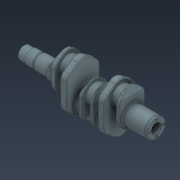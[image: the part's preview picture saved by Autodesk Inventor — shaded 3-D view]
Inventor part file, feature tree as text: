
AUTODESK INVENTOR PART (.ipt)
format: ipt  version: 2022 (Build 260153000, 153)  size: 985,088 bytes
history: native  units: mm
features: sketch x21, extrude x17, plane x4, hole x3, chamfer x3, projected_geometry x3, revolve x2, fillet x2, mirror x2
ambient origin geometry x8: Origin, YZ Plane, XZ Plane, XY Plane, X Axis, Y Axis, Z Axis, Center Point
bodies: Solid1 (feature_tree)
feature tree (57):
  revolve  "Revolution1"  [1 undecoded]
  plane  "Work Plane7"
  sketch  "Sketch22"  dims[d3=44.0mm d4=36.0mm]
  extrude  "Extrusion18"  Depth=36.0mm
  extrude  "Extrusion19"  Depth=42.0mm
  extrude  "Extrusion20"  Depth=2.0mm
  extrude  "Extrusion21"  TaperAngle=90.0deg  [1 undecoded]
  plane  "Work Plane8"
  extrude  "Extrusion22"  Depth=1.0mm
  extrude  "Extrusion23"  Depth=65.0mm
  extrude  "Extrusion24"  Depth=34.5mm
  extrude  "Extrusion25"  Depth=1.0mm TaperAngle=0.0deg
  extrude  "Extrusion26"  Depth=74.0mm
  extrude  "Extrusion27"  Depth=51.2mm
  extrude  "Extrusion28"  Depth=10.0mm TaperAngle=0.0deg
  plane  "Work Plane9"
  extrude  "Extrusion29"  Depth=1.0mm
  extrude  "Extrusion30"  Depth=1.0mm
  fillet  "Fillet1"  Radius=1.0mm
  mirror  "Mirror1"
  mirror  "Mirror2"
  plane  "Work Plane10"
  extrude  "Extrusion32"  Depth=29.9mm
  extrude  "Extrusion33"  Depth=1.0mm TaperAngle=0.0deg
  extrude  "Extrusion34"  Depth=2.0mm
  extrude  "Extrusion35"  Depth=21.0mm TaperAngle=0.0deg
  fillet  "Fillet2"  Radius=1.0mm
  revolve  "Revolution2"  [1 undecoded]
  hole  "Hole1"  [1 undecoded]
  hole  "Hole2"  [1 undecoded]
  hole  "Hole3"  [1 undecoded]
  chamfer  "Chamfer1"  Distance=55.0mm
  chamfer  "Chamfer2"  Distance=21.0mm
  chamfer  "Chamfer3"  Distance=28.965484mm
  sketch  "Sketch1"  dims[d1=23.0mm d2=23.0mm]
  sketch  "Sketch23"  dims[d6=40.0mm d7=42.0mm]
  sketch  "Sketch24"  dims[d9=25.5mm d10=2.0mm]
  sketch  "Sketch25"  dims[d11=1.5mm d12=90.0deg]
  sketch  "Sketch26"  dims[d13=65.0mm d15=1.0mm]
  sketch  "Sketch27"  dims[d96=14.76mm d97=65.0mm]
  sketch  "Sketch28"  dims[d98=55.0mm d99=34.5mm]
  sketch  "Sketch29"  dims[d100=22.0mm d101=0.0mm d102=1.0mm d103=0.0mm]
  sketch  "Sketch30"  dims[d105=15.0mm d106=74.0mm]
  projected_geometry  "Projected Loop9"
  sketch  "Sketch31"  dims[d107=27.2mm d108=51.2mm]
  sketch  "Sketch32"  dims[d109=2.0mm d110=10.0mm d111=0.0mm]
  sketch  "Sketch33"  dims[d112=1.0mm d113=0.0mm d114=18.91mm]
  sketch  "Sketch35"  dims[d115=65.0mm d116=69.0mm d117=1.0mm d118=0.0mm]
  sketch  "Sketch36"  dims[d119=25.0mm d120=29.9mm]
  sketch  "Sketch37"  dims[d122=95.0mm d124=1.0mm d125=0.0mm]
  sketch  "Sketch39"  dims[d126=2.0mm d127=2.0mm]
  projected_geometry  "Projected Loop12"
  projected_geometry  "Projected Loop13"
  sketch  "Sketch40"  dims[d128=55.0mm d129=21.0mm d130=0.0mm d131=1.0mm d132=0.0mm]
  sketch  "Sketch41"  dims[d133=15.0mm d134=25.0mm]
  sketch  "Sketch42"  dims[d135=40.4mm d136=25.0mm]
  sketch  "Sketch43"  dims[d137=10.43mm d138=0.0mm d139=65.0mm d140=1.0mm d141=0.0mm d142=55.0mm d143=21.0mm d144=0.0mm d145=28.965484mm d146=23.0mm d147=0.0mm d148=0.0mm d149=28.965484mm d150=8.0mm d151=10.0mm d152=0.0mm d153=2.0mm d156=10.27mm d157=70.0mm d158=1.0mm d159=0.0mm d160=1.0mm d161=0.0mm d162=28.965484mm d163=23.0mm d164=10.0mm d165=0.0mm d166=0.0mm d167=0.0mm d168=2.0mm d171=53.0mm d172=50.0mm d173=2.0mm d175=21.0mm d176=100.0mm d177=55.0mm d178=68.118mm d179=2.0mm d180=58.0mm d181=3.0mm d182=2.0mm d183=5.0mm d184=90.0deg d185=17.294mm d186=30.7mm d187=20.4mm d188=4.0mm d189=90.0deg d190=30.7mm d191=20.594885mm d192=25.834936mm d193=21.5mm d194=28.3mm d195=5.75mm d196=90.0deg d197=21.5mm d198=20.594885mm d199=1.0mm d200=2.0mm d201=45.0deg d202=1.5mm d203=2.0mm d204=45.0deg d205=2.0mm d206=2.0mm d207=45.0deg d208=41.0mm d209=6.647mm d210=12.4mm d211=28.3mm d212=5.75mm d213=90.0deg d214=12.4mm d215=20.594885mm d41=0.5mm d42=0.872665mm d43=0.5mm d44=0.872665mm d91=0.5mm d92=0.872665mm d93=0.5mm d94=0.872665mm]
note: 6 required parameter values undecoded (feature->parameter linkage not recoverable at this tier; creation-order binding heuristic only, values carry confidence <= 0.55)